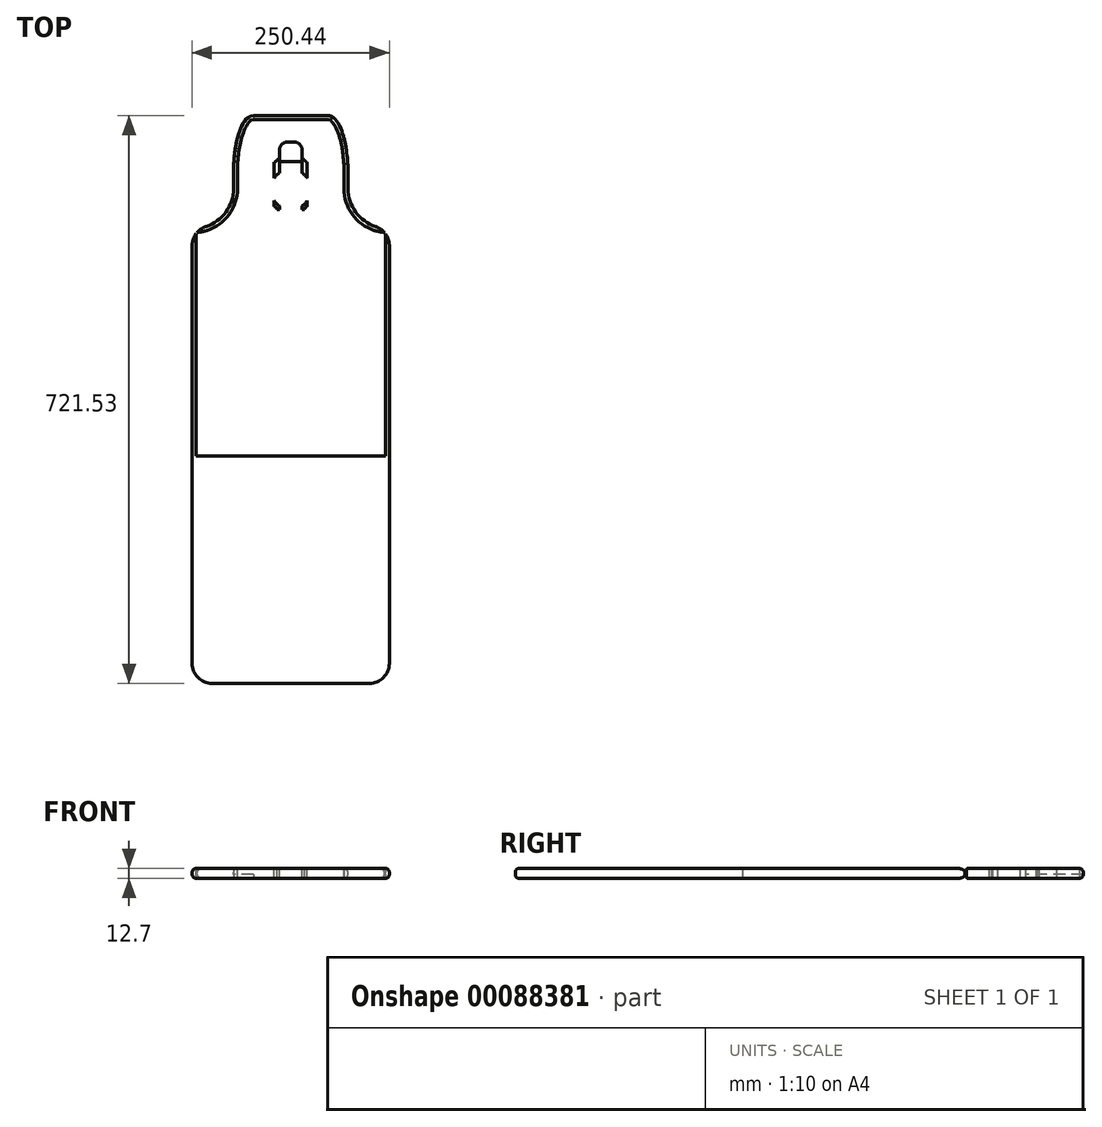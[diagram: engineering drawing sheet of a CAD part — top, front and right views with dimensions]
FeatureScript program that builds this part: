
annotation { "Feature Type Name" : "Feature", "Feature Type Description" : "" }
export const myFeature = defineFeature(function(context is Context, id is Id, definition is map)
    precondition{}
    {
        {
            var Q0;
            Q0=qCreatedBy(makeId("Top.planeOp"),FACE);
            var sketch = newSketch(context, id + "F0", { "sketchPlane" : qUnion([Q0])});
            skLineSegment(sketch, "E0.bottom", {"start": v(-117.17, 288.93) * mm, "end": v(-125.22, 288.93) * mm});
            skLineSegment(sketch, "E0.top", {"start": v(125.22, -288.93) * mm, "end": v(-125.22, -288.93) * mm});
            skLineSegment(sketch, "E0.left", {"start": v(125.22, 288.93) * mm, "end": v(125.22, -288.93) * mm});
            skLineSegment(sketch, "E0.right", {"start": v(-125.22, 288.93) * mm, "end": v(-125.22, -288.93) * mm});
            skPoint(sketch, "E0.middle", {"position": v(0, 0) * mm});
            skLineSegment(sketch, "E1", {"start": v(0, 308.77) * mm, "end": v(0, 432.6) * mm});
            skLineSegment(sketch, "E2.bottom", {"start": v(0, 432.6) * mm, "end": v(-47.32, 432.6) * mm});
            skLineSegment(sketch, "E2.right", {"start": v(-72.72, 360.76) * mm, "end": v(-72.72, 333.38) * mm});
            skLineSegment(sketch, "E3", {"start": v(0, 432.6) * mm, "end": v(0, 372.27) * mm});
            skLineSegment(sketch, "E4", {"start": v(-125.22, 0) * mm, "end": v(125.22, 0) * mm});
            skEllipticalArc(sketch, "E5", {});
            skPoint(sketch, "E6.newPointA", {"position": v(125.22, 288.93) * mm});
            skPoint(sketch, "E7.orphan", {"position": v(-72.72, 432.6) * mm});
            skLineSegment(sketch, "E8", {"start": v(125.22, 288.93) * mm, "end": v(117.17, 288.93) * mm});
            skPoint(sketch, "E2.left.start.orphan", {"position": v(72.72, 432.6) * mm});
            skEllipticalArc(sketch, "E9.MirrorCS", {});
            skLineSegment(sketch, "E10.MirrorCS", {"start": v(72.72, 360.76) * mm, "end": v(72.72, 333.38) * mm});
            skLineSegment(sketch, "E11.MirrorCS", {"start": v(0, 432.6) * mm, "end": v(47.32, 432.6) * mm});
            skLineSegment(sketch, "E12.MirrorCS", {"start": v(117.17, 288.93) * mm, "end": v(125.22, 288.93) * mm});
            skPoint(sketch, "E13.orphan", {"position": v(72.72, 288.93) * mm});
            skPoint(sketch, "E2.top.end.orphan", {"position": v(-72.72, 288.93) * mm});
            skLineSegment(sketch, "E14", {"start": v(-123.52, 288.93) * mm, "end": v(-117.17, 288.93) * mm});
            skLineSegment(sketch, "E15", {"start": v(-72.72, 333.38) * mm, "end": v(-72.72, 339.73) * mm});
            skLineSegment(sketch, "E16", {"start": v(117.17, 288.93) * mm, "end": v(123.52, 288.93) * mm});
            skLineSegment(sketch, "E17", {"start": v(72.72, 333.38) * mm, "end": v(72.72, 339.73) * mm});
            skArc(sketch, "E18.filletArc", {"start": v(-123.52, 288.92) * mm, "mid": v(-87.6, 303.8) * mm, "end": v(-72.72, 339.73) * mm});
            skArc(sketch, "E19.filletArc", {"start": v(72.72, 339.73) * mm, "mid": v(87.6, 303.8) * mm, "end": v(123.52, 288.93) * mm});
            skEllipticalArc(sketch, "E20.MirrorCS", {});
            skEllipticalArc(sketch, "E21.MirrorCS", {});
            skLineSegment(sketch, "E22.MirrorCS", {"start": v(72.72, -360.76) * mm, "end": v(72.72, -333.38) * mm});
            skArc(sketch, "E23.MirrorCS", {"start": v(72.72, -339.73) * mm, "mid": v(87.6, -303.8) * mm, "end": v(123.52, -288.92) * mm});
            skLineSegment(sketch, "E24.MirrorCS", {"start": v(117.17, -288.92) * mm, "end": v(123.52, -288.92) * mm});
            skLineSegment(sketch, "E25.MirrorCS", {"start": v(0, -432.6) * mm, "end": v(47.32, -432.6) * mm});
            skLineSegment(sketch, "E26.MirrorCS", {"start": v(0, -432.6) * mm, "end": v(-47.32, -432.6) * mm});
            skArc(sketch, "E27.MirrorCS", {"start": v(-123.52, -288.93) * mm, "mid": v(-87.6, -303.8) * mm, "end": v(-72.72, -339.73) * mm});
            skLineSegment(sketch, "E28.MirrorCS", {"start": v(-123.52, -288.93) * mm, "end": v(-117.17, -288.93) * mm});
            skLineSegment(sketch, "E29.MirrorCS", {"start": v(-117.17, -288.93) * mm, "end": v(-125.22, -288.93) * mm});
            skLineSegment(sketch, "E30.MirrorCS", {"start": v(-72.72, -360.76) * mm, "end": v(-72.72, -333.38) * mm});
            skLineSegment(sketch, "E31", {"start": v(-125.22, 288.93) * mm, "end": v(125.22, 288.93) * mm});
            const initialGuessF0  = {"E5": [-0.04731550595760356, 0.3607635015405606, 0, 1, 0.071834375, 0.0254, 0, 1.5707963267948966], "E9.MirrorCS": [0.04731550595760346, 0.3607635015405606, 0, 1, 0.071834375, 0.0254, 4.71238898038469, 0], "E20.MirrorCS": [-0.0473155059576034, -0.3607635015405606, 0, -1, 0.071834375, 0.0254, 4.71238898038469, 0], "E21.MirrorCS": [0.04731550595760362, -0.3607635015405606, 0, -1, 0.071834375, 0.0254, 0, 1.5707963267948966], "E20.MirrorCS": [-0.0473155059576034, -0.3607635015405606, 0, -1, 0.071834375, 0.0254, 4.71238898038469, 0], "E21.MirrorCS": [0.04731550595760362, -0.3607635015405606, 0, -1, 0.071834375, 0.0254, 0, 1.5707963267948966]};
            skSetInitialGuess(sketch, initialGuessF0);
            skSolve(sketch);
        }
        {
            var Q0;
            Q0=makeQuery(id+"F0.imprint","IMPRINT",FACE,{"disambiguationData":[TD([[makeQuery(id+"F0.imprint","IMPRINT",EDGE,{"derivedFrom":sQuery(id+"F0.wireOp",EDGE,"E2.bottom")}),1.0]])]});
            var Q1;
            {var subQ4=sQuery(id+"F0.wireOp",EDGE,"E4");Q1=makeQuery(id+"F0.imprint","IMPRINT",FACE,{"disambiguationData":[TD([[makeQuery(id+"F0.imprint","IMPRINT",EDGE,{"derivedFrom":subQ4}),1.0]])]});}
            var Q2;
            {var subQ3=sQuery(id+"F0.wireOp",EDGE,"E4");Q2=makeQuery(id+"F0.imprint","IMPRINT",FACE,{"disambiguationData":[TD([[makeQuery(id+"F0.imprint","IMPRINT",EDGE,{"derivedFrom":subQ3}),-1.0]])]});}
            var Q3;
            {var subQ6=sQuery(id+"F0.wireOp",EDGE,"E23.MirrorCS");Q3=makeQuery(id+"F0.imprint","IMPRINT",FACE,{"disambiguationData":[TD([[makeQuery(id+"F0.imprint","IMPRINT",EDGE,{"derivedFrom":subQ6}),1.0]])]});}
            extrude(context, id + "F1", {"entities" : qUnion([Q0, Q1, Q2, Q3]), "oppositeDirection" : true, "depth" : 12.7 * mm});
        }
        {
            var Q0;
            Q0=makeQuery(id+"F1.opExtrude","CAP_FACE",FACE,{"disambiguationData":[OSD([sQuery(id+"F0.wireOp",EDGE,"E0.top"),sQuery(id+"F0.wireOp",EDGE,"E0.left"),sQuery(id+"F0.wireOp",EDGE,"E0.right"),sQuery(id+"F0.wireOp",EDGE,"E2.bottom"),sQuery(id+"F0.wireOp",EDGE,"E2.right"),sQuery(id+"F0.wireOp",EDGE,"E5"),sQuery(id+"F0.wireOp",EDGE,"E9.MirrorCS"),sQuery(id+"F0.wireOp",EDGE,"E10.MirrorCS"),sQuery(id+"F0.wireOp",EDGE,"E11.MirrorCS"),sQuery(id+"F0.wireOp",EDGE,"E18.filletArc"),sQuery(id+"F0.wireOp",EDGE,"E19.filletArc"),sQuery(id+"F0.wireOp",EDGE,"E23.MirrorCS"),sQuery(id+"F0.wireOp",EDGE,"E25.MirrorCS"),sQuery(id+"F0.wireOp",EDGE,"E26.MirrorCS"),sQuery(id+"F0.wireOp",EDGE,"E20.MirrorCS"),sQuery(id+"F0.wireOp",EDGE,"E21.MirrorCS"),sQuery(id+"F0.wireOp",EDGE,"E22.MirrorCS"),sQuery(id+"F0.wireOp",EDGE,"E27.MirrorCS"),sQuery(id+"F0.wireOp",EDGE,"E29.MirrorCS"),sQuery(id+"F0.wireOp",EDGE,"E30.MirrorCS"),sQuery(id+"F0.wireOp",EDGE,"E31")])],"isStart":true});
            var Q1;
            Q1=makeQuery(id+"F1.opExtrude","CAP_FACE",FACE,{"disambiguationData":[OSD([sQuery(id+"F0.wireOp",EDGE,"E0.top"),sQuery(id+"F0.wireOp",EDGE,"E0.left"),sQuery(id+"F0.wireOp",EDGE,"E0.right"),sQuery(id+"F0.wireOp",EDGE,"E2.bottom"),sQuery(id+"F0.wireOp",EDGE,"E2.right"),sQuery(id+"F0.wireOp",EDGE,"E5"),sQuery(id+"F0.wireOp",EDGE,"E9.MirrorCS"),sQuery(id+"F0.wireOp",EDGE,"E10.MirrorCS"),sQuery(id+"F0.wireOp",EDGE,"E11.MirrorCS"),sQuery(id+"F0.wireOp",EDGE,"E18.filletArc"),sQuery(id+"F0.wireOp",EDGE,"E19.filletArc"),sQuery(id+"F0.wireOp",EDGE,"E23.MirrorCS"),sQuery(id+"F0.wireOp",EDGE,"E25.MirrorCS"),sQuery(id+"F0.wireOp",EDGE,"E26.MirrorCS"),sQuery(id+"F0.wireOp",EDGE,"E20.MirrorCS"),sQuery(id+"F0.wireOp",EDGE,"E21.MirrorCS"),sQuery(id+"F0.wireOp",EDGE,"E22.MirrorCS"),sQuery(id+"F0.wireOp",EDGE,"E27.MirrorCS"),sQuery(id+"F0.wireOp",EDGE,"E29.MirrorCS"),sQuery(id+"F0.wireOp",EDGE,"E30.MirrorCS"),sQuery(id+"F0.wireOp",EDGE,"E31")])],"isStart":false});
            fillet(context, id + "F2", {"entities" : qUnion([Q0, Q1]), "radius" : 5.08 * mm, "tangentPropagation" : true, "allowEdgeOverflow" : false});
        }
        {
            var Q0;
            Q0=makeQuery(id+"F1.opExtrude","CAP_FACE",FACE,{"disambiguationData":[OSD([sQuery(id+"F0.wireOp",EDGE,"E0.top"),sQuery(id+"F0.wireOp",EDGE,"E0.left"),sQuery(id+"F0.wireOp",EDGE,"E0.right"),sQuery(id+"F0.wireOp",EDGE,"E2.bottom"),sQuery(id+"F0.wireOp",EDGE,"E2.right"),sQuery(id+"F0.wireOp",EDGE,"E5"),sQuery(id+"F0.wireOp",EDGE,"E9.MirrorCS"),sQuery(id+"F0.wireOp",EDGE,"E10.MirrorCS"),sQuery(id+"F0.wireOp",EDGE,"E11.MirrorCS"),sQuery(id+"F0.wireOp",EDGE,"E18.filletArc"),sQuery(id+"F0.wireOp",EDGE,"E19.filletArc"),sQuery(id+"F0.wireOp",EDGE,"E23.MirrorCS"),sQuery(id+"F0.wireOp",EDGE,"E25.MirrorCS"),sQuery(id+"F0.wireOp",EDGE,"E26.MirrorCS"),sQuery(id+"F0.wireOp",EDGE,"E20.MirrorCS"),sQuery(id+"F0.wireOp",EDGE,"E21.MirrorCS"),sQuery(id+"F0.wireOp",EDGE,"E22.MirrorCS"),sQuery(id+"F0.wireOp",EDGE,"E27.MirrorCS"),sQuery(id+"F0.wireOp",EDGE,"E29.MirrorCS"),sQuery(id+"F0.wireOp",EDGE,"E30.MirrorCS"),sQuery(id+"F0.wireOp",EDGE,"E31")])],"isStart":true});
            var sketch = newSketch(context, id + "F3", { "sketchPlane" : qUnion([Q0])});
            skLineSegment(sketch, "E32", {"start": v(0, 427.52) * mm, "end": v(0, 376.72) * mm});
            skPoint(sketch, "E32.endSnap0", {"position": v(0, 427.52) * mm});
            skLineSegment(sketch, "E33", {"start": v(0, 376.72) * mm, "end": v(-20.96, 376.72) * mm});
            skLineSegment(sketch, "E34.bottom", {"start": v(-20.96, 376.72) * mm, "end": v(20.96, 376.72) * mm});
            skLineSegment(sketch, "E34.top", {"start": v(-20.95, 313.22) * mm, "end": v(20.96, 313.22) * mm});
            skLineSegment(sketch, "E34.left", {"start": v(-20.96, 376.72) * mm, "end": v(-20.96, 313.22) * mm});
            skLineSegment(sketch, "E34.right", {"start": v(20.96, 376.72) * mm, "end": v(20.96, 313.22) * mm});
            skLineSegment(sketch, "E35.0", {"start": v(-18.57, 374.34) * mm, "end": v(18.57, 374.34) * mm});
            skLineSegment(sketch, "E35.1", {"start": v(-18.57, 374.34) * mm, "end": v(-18.57, 315.6) * mm});
            skLineSegment(sketch, "E35.2", {"start": v(-18.57, 315.6) * mm, "end": v(18.57, 315.6) * mm});
            skLineSegment(sketch, "E35.3", {"start": v(18.57, 374.34) * mm, "end": v(18.57, 315.6) * mm});
            skCircle(sketch, "E36", {"center": v(-20.96, 376.72) * mm, "radius": 3.37 * mm});
            skCircle(sketch, "E37", {"center": v(20.96, 376.72) * mm, "radius": 3.37 * mm});
            skCircle(sketch, "E38", {"center": v(-20.95, 313.22) * mm, "radius": 3.37 * mm});
            skCircle(sketch, "E39", {"center": v(20.96, 313.22) * mm, "radius": 3.37 * mm});
            skLineSegment(sketch, "E40", {"start": v(-120.14, 0) * mm, "end": v(120.14, 0) * mm});
            skCircle(sketch, "E41.MirrorC", {"center": v(-20.95, -376.72) * mm, "radius": 3.37 * mm});
            skCircle(sketch, "E42.MirrorC", {"center": v(20.96, -313.22) * mm, "radius": 3.37 * mm});
            skCircle(sketch, "E43.MirrorC", {"center": v(-20.95, -313.22) * mm, "radius": 3.37 * mm});
            skCircle(sketch, "E44.MirrorC", {"center": v(20.96, -376.72) * mm, "radius": 3.37 * mm});
            skLineSegment(sketch, "E45", {"start": v(20.96, -313.22) * mm, "end": v(-20.95, -313.22) * mm});
            skLineSegment(sketch, "E46", {"start": v(0, -313.22) * mm, "end": v(0, -297.34) * mm});
            skLineSegment(sketch, "E47", {"start": v(0, -297.34) * mm, "end": v(-7.94, -297.34) * mm});
            skLineSegment(sketch, "E48", {"start": v(0, -297.34) * mm, "end": v(0, -398.94) * mm});
            skLineSegment(sketch, "E49", {"start": v(0, -398.94) * mm, "end": v(4.13, -398.94) * mm});
            skLineSegment(sketch, "E50.bottom", {"start": v(-7.94, -297.34) * mm, "end": v(7.94, -297.34) * mm});
            skLineSegment(sketch, "E50.top", {"start": v(-4.13, -398.94) * mm, "end": v(4.13, -398.94) * mm});
            skLineSegment(sketch, "E50.left", {"start": v(-14.29, -303.7) * mm, "end": v(-14.29, -317.62) * mm});
            skLineSegment(sketch, "E50.right", {"start": v(14.29, -303.7) * mm, "end": v(14.29, -317.62) * mm});
            skLineSegment(sketch, "E51", {"start": v(0, -313.22) * mm, "end": v(0, -338.62) * mm});
            skArc(sketch, "E52", {"start": v(-14.29, -317.62) * mm, "mid": v(-25.4, -338.62) * mm, "end": v(-14.29, -359.62) * mm});
            skArc(sketch, "E53.trimOffspring", {"start": v(14.29, -359.62) * mm, "mid": v(25.4, -338.62) * mm, "end": v(14.29, -317.62) * mm});
            skPoint(sketch, "E54.visualSharp", {"position": v(14.29, -398.94) * mm});
            skArc(sketch, "E54.filletArc", {"start": v(4.13, -398.94) * mm, "mid": v(11.31, -395.97) * mm, "end": v(14.29, -388.78) * mm});
            skPoint(sketch, "E55.visualSharp", {"position": v(-14.29, -398.94) * mm});
            skArc(sketch, "E55.filletArc", {"start": v(-14.29, -388.78) * mm, "mid": v(-11.31, -395.97) * mm, "end": v(-4.13, -398.94) * mm});
            skPoint(sketch, "E56.visualSharp", {"position": v(-14.29, -297.34) * mm});
            skArc(sketch, "E56.filletArc", {"start": v(-7.94, -297.34) * mm, "mid": v(-12.43, -299.2) * mm, "end": v(-14.29, -303.7) * mm});
            skPoint(sketch, "E57.visualSharp", {"position": v(14.29, -297.34) * mm});
            skArc(sketch, "E57.filletArc", {"start": v(14.29, -303.7) * mm, "mid": v(12.43, -299.2) * mm, "end": v(7.94, -297.34) * mm});
            skLineSegment(sketch, "E58.trimOffspring", {"start": v(14.29, -359.62) * mm, "end": v(14.29, -388.78) * mm});
            skLineSegment(sketch, "E59.trimOffspring", {"start": v(-14.29, -359.62) * mm, "end": v(-14.29, -388.78) * mm});
            skArc(sketch, "E60.MirrorCS", {"start": v(14.29, 359.62) * mm, "mid": v(25.4, 338.62) * mm, "end": v(14.29, 317.62) * mm});
            skArc(sketch, "E61.MirrorCS", {"start": v(-14.29, 317.62) * mm, "mid": v(-25.4, 338.62) * mm, "end": v(-14.29, 359.62) * mm});
            skLineSegment(sketch, "E62.MirrorCS", {"start": v(-14.29, 359.62) * mm, "end": v(-14.29, 388.78) * mm});
            skLineSegment(sketch, "E63.MirrorCS", {"start": v(14.29, 359.62) * mm, "end": v(14.29, 388.78) * mm});
            skArc(sketch, "E64.MirrorCS", {"start": v(4.13, 398.94) * mm, "mid": v(11.31, 395.97) * mm, "end": v(14.29, 388.78) * mm});
            skArc(sketch, "E65.MirrorCS", {"start": v(-14.29, 388.78) * mm, "mid": v(-11.31, 395.97) * mm, "end": v(-4.13, 398.94) * mm});
            skLineSegment(sketch, "E66.MirrorCS", {"start": v(-4.13, 398.94) * mm, "end": v(4.13, 398.94) * mm});
            skLineSegment(sketch, "E67.MirrorCS", {"start": v(-7.94, 297.34) * mm, "end": v(7.94, 297.34) * mm});
            skArc(sketch, "E68.MirrorCS", {"start": v(14.29, 303.7) * mm, "mid": v(12.43, 299.2) * mm, "end": v(7.94, 297.34) * mm});
            skArc(sketch, "E69.MirrorCS", {"start": v(-7.94, 297.34) * mm, "mid": v(-12.43, 299.2) * mm, "end": v(-14.29, 303.7) * mm});
            skLineSegment(sketch, "E70.MirrorCS", {"start": v(-14.29, 303.7) * mm, "end": v(-14.29, 317.62) * mm});
            skLineSegment(sketch, "E71.MirrorCS", {"start": v(14.29, 303.7) * mm, "end": v(14.29, 317.62) * mm});
            skSolve(sketch);
        }
        {
            var Q0;
            Q0=sQuery(id+"F3.wireOp",VERTEX,"3598a4d0-b501-495c-ae59-4652df5df4007.MirrorCS.end");
            var Q1;
            Q1=sQuery(id+"F3.wireOp",VERTEX,"3598a4d0-b501-495c-ae59-4652df5df4008.MirrorCS.end");
            var Q2;
            Q2=sQuery(id+"F3.wireOp",VERTEX,"3598a4d0-b501-495c-ae59-4652df5df4004.MirrorCS.end");
            var Q3;
            Q3=sQuery(id+"F3.wireOp",VERTEX,"3598a4d0-b501-495c-ae59-4652df5df4009.MirrorCS.start");
            var Q4;
            Q4=sQuery(id+"F3.wireOp",VERTEX,"E37.center");
            var Q5;
            Q5=sQuery(id+"F3.wireOp",VERTEX,"E34.left.start");
            var Q6;
            Q6=sQuery(id+"F3.wireOp",VERTEX,"E38.center");
            var Q7;
            Q7=sQuery(id+"F3.wireOp",VERTEX,"E34.right.end");
            var Q8;
            Q8=sQuery(id+"F3.wireOp",VERTEX,"E42.MirrorC.center");
            var Q9;
            Q9=sQuery(id+"F3.wireOp",VERTEX,"E43.MirrorC.center");
            var Q10;
            Q10=sQuery(id+"F3.wireOp",VERTEX,"E44.MirrorC.center");
            var Q11;
            Q11=sQuery(id+"F3.wireOp",VERTEX,"E41.MirrorC.center");
            var Q12;
            Q12=makeQuery(id+"F1.opExtrude","SWEPT_BODY",BODY,{"disambiguationData":[OSD([sQuery(id+"F0.wireOp",EDGE,"E0.top"),sQuery(id+"F0.wireOp",EDGE,"E0.left"),sQuery(id+"F0.wireOp",EDGE,"E0.right"),sQuery(id+"F0.wireOp",EDGE,"E2.bottom"),sQuery(id+"F0.wireOp",EDGE,"E2.right"),sQuery(id+"F0.wireOp",EDGE,"E5"),sQuery(id+"F0.wireOp",EDGE,"E9.MirrorCS"),sQuery(id+"F0.wireOp",EDGE,"E10.MirrorCS"),sQuery(id+"F0.wireOp",EDGE,"E11.MirrorCS"),sQuery(id+"F0.wireOp",EDGE,"E18.filletArc"),sQuery(id+"F0.wireOp",EDGE,"E19.filletArc"),sQuery(id+"F0.wireOp",EDGE,"E23.MirrorCS"),sQuery(id+"F0.wireOp",EDGE,"E25.MirrorCS"),sQuery(id+"F0.wireOp",EDGE,"E26.MirrorCS"),sQuery(id+"F0.wireOp",EDGE,"E20.MirrorCS"),sQuery(id+"F0.wireOp",EDGE,"E21.MirrorCS"),sQuery(id+"F0.wireOp",EDGE,"E22.MirrorCS"),sQuery(id+"F0.wireOp",EDGE,"E27.MirrorCS"),sQuery(id+"F0.wireOp",EDGE,"E29.MirrorCS"),sQuery(id+"F0.wireOp",EDGE,"E30.MirrorCS"),sQuery(id+"F0.wireOp",EDGE,"E31")])]});
            hole(context, id + "F4", {"style" : HoleStyle.SIMPLE, "endStyle" : HoleEndStyle.THROUGH, "standardTappedOrClearance" : lookupTablePath({ "standard" : "ANSI", "fit" : "Normal (ASME)", "size" : "1/4", "type" : "Clearance" }), "standardBlindInLast" : lookupTablePath({ "fit" : "Free", "standard" : "ANSI", "size" : "1/4", "type" : "Clearance" }), "holeDiameter" : 6.76 * mm, "locations" : qUnion([Q0, Q1, Q2, Q3, Q4, Q5, Q6, Q7, Q8, Q9, Q10, Q11]), "scope" : qUnion([Q12]), "isTappedThrough" : true});
        }
        {
            var Q0;
            Q0=makeQuery(id+"F1.opExtrude","SWEPT_EDGE",EDGE,{"disambiguationData":[OSD([sQuery(id+"F0.wireOp",EDGE,"E0.right"),sQuery(id+"F0.wireOp",EDGE,"E31")])]});
            var Q1;
            Q1=makeQuery(id+"F1.opExtrude","SWEPT_EDGE",EDGE,{"disambiguationData":[OSD([sQuery(id+"F0.wireOp",EDGE,"E0.left"),sQuery(id+"F0.wireOp",EDGE,"E31")])]});
            var Q2;
            Q2=makeQuery(id+"F1.opExtrude","SWEPT_EDGE",EDGE,{"disambiguationData":[OSD([sQuery(id+"F0.wireOp",EDGE,"E0.top"),sQuery(id+"F0.wireOp",EDGE,"E0.left")])]});
            var Q3;
            Q3=makeQuery(id+"F1.opExtrude","SWEPT_EDGE",EDGE,{"disambiguationData":[OSD([sQuery(id+"F0.wireOp",EDGE,"E0.right"),sQuery(id+"F0.wireOp",EDGE,"E29.MirrorCS")])]});
            fillet(context, id + "F5", {"entities" : qUnion([Q0, Q1, Q2, Q3]), "radius" : 25.4 * mm, "tangentPropagation" : true, "allowEdgeOverflow" : false});
        }
        {
            var Q0;
            {var subQ3=sQuery(id+"F3.wireOp",EDGE,"E35.0");var subQ5=sQuery(id+"F3.wireOp",EDGE,"E62.MirrorCS");var subQ8=makeQuery(id+"F3.imprint","INTERSECT",VERTEX,{"derivedFrom":[subQ3,subQ5]});Q0=makeQuery(id+"F3.imprint","IMPRINT",FACE,{"disambiguationData":[TD([[makeQuery(id+"F3.imprint","IMPRINT",EDGE,{"disambiguationData":[TD([[subQ8,-1.0]])],"derivedFrom":subQ3}),-1.0]])]});}
            var Q1;
            {var subQ1=sQuery(id+"F3.wireOp",EDGE,"E34.bottom");var subQ5=makeQuery(id+"F3.imprint","INTERSECT",VERTEX,{"derivedFrom":[sQuery(id+"F3.wireOp",EDGE,"E32"),subQ1]});Q1=makeQuery(id+"F3.imprint","IMPRINT",FACE,{"disambiguationData":[TD([[makeQuery(id+"F3.imprint","IMPRINT",EDGE,{"disambiguationData":[TD([[subQ5,1.0]])],"derivedFrom":subQ1}),-1.0]])]});}
            var Q2;
            {var subQ0=sQuery(id+"F3.wireOp",EDGE,"E64.MirrorCS");Q2=makeQuery(id+"F3.imprint","IMPRINT",FACE,{"disambiguationData":[TD([[makeQuery(id+"F3.imprint","IMPRINT",EDGE,{"derivedFrom":subQ0}),-1.0]])]});}
            var Q3;
            {var subQ0=sQuery(id+"F3.wireOp",EDGE,"E65.MirrorCS");Q3=makeQuery(id+"F3.imprint","IMPRINT",FACE,{"disambiguationData":[TD([[makeQuery(id+"F3.imprint","IMPRINT",EDGE,{"derivedFrom":subQ0}),-1.0]])]});}
            var Q4;
            {var subQ0=sQuery(id+"F3.wireOp",EDGE,"E60.MirrorCS");var subQ1=sQuery(id+"F3.wireOp",EDGE,"E34.right");var subQ2=makeQuery(id+"F3.imprint","INTERSECT",VERTEX,{"disambiguationData":[OD(0.0)],"derivedFrom":[subQ1,subQ0]});Q4=makeQuery(id+"F3.imprint","IMPRINT",FACE,{"disambiguationData":[TD([[makeQuery(id+"F3.imprint","IMPRINT",EDGE,{"disambiguationData":[TD([[subQ2,-1.0]])],"derivedFrom":subQ1}),-1.0]])]});}
            var Q5;
            {var subQ0=sQuery(id+"F3.wireOp",EDGE,"E60.MirrorCS");var subQ1=sQuery(id+"F3.wireOp",EDGE,"E34.right");var subQ2=makeQuery(id+"F3.imprint","INTERSECT",VERTEX,{"disambiguationData":[OD(0.0)],"derivedFrom":[subQ1,subQ0]});Q5=makeQuery(id+"F3.imprint","IMPRINT",FACE,{"disambiguationData":[TD([[makeQuery(id+"F3.imprint","IMPRINT",EDGE,{"disambiguationData":[TD([[subQ2,-1.0]])],"derivedFrom":subQ1}),1.0]])]});}
            var Q6;
            {var subQ0=sQuery(id+"F3.wireOp",EDGE,"E61.MirrorCS");var subQ1=sQuery(id+"F3.wireOp",EDGE,"E34.left");var subQ2=makeQuery(id+"F3.imprint","INTERSECT",VERTEX,{"disambiguationData":[OD(0.0)],"derivedFrom":[subQ1,subQ0]});Q6=makeQuery(id+"F3.imprint","IMPRINT",FACE,{"disambiguationData":[TD([[makeQuery(id+"F3.imprint","IMPRINT",EDGE,{"disambiguationData":[TD([[subQ2,-1.0]])],"derivedFrom":subQ1}),1.0]])]});}
            var Q7;
            {var subQ0=sQuery(id+"F3.wireOp",EDGE,"E61.MirrorCS");var subQ1=sQuery(id+"F3.wireOp",EDGE,"E34.left");var subQ2=makeQuery(id+"F3.imprint","INTERSECT",VERTEX,{"disambiguationData":[OD(0.0)],"derivedFrom":[subQ1,subQ0]});Q7=makeQuery(id+"F3.imprint","IMPRINT",FACE,{"disambiguationData":[TD([[makeQuery(id+"F3.imprint","IMPRINT",EDGE,{"disambiguationData":[TD([[subQ2,-1.0]])],"derivedFrom":subQ1}),-1.0]])]});}
            var Q8;
            Q8=makeQuery(id+"F3.imprint","IMPRINT",FACE,{"disambiguationData":[TD([[makeQuery(id+"F3.imprint","IMPRINT",EDGE,{"derivedFrom":sQuery(id+"F3.wireOp",EDGE,"E67.MirrorCS")}),1.0]])]});
            var Q9;
            {var subQ0=sQuery(id+"F3.wireOp",EDGE,"E70.MirrorCS");var subQ1=sQuery(id+"F3.wireOp",EDGE,"E34.top");var subQ2=makeQuery(id+"F3.imprint","INTERSECT",VERTEX,{"derivedFrom":[subQ1,subQ0]});Q9=makeQuery(id+"F3.imprint","IMPRINT",FACE,{"disambiguationData":[TD([[makeQuery(id+"F3.imprint","IMPRINT",EDGE,{"disambiguationData":[TD([[subQ2,-1.0]])],"derivedFrom":subQ1}),1.0]])]});}
            var Q10;
            {var subQ4=sQuery(id+"F3.wireOp",EDGE,"E51");Q10=makeQuery(id+"F3.imprint","IMPRINT",FACE,{"disambiguationData":[TD([[makeQuery(id+"F3.imprint","IMPRINT",EDGE,{"derivedFrom":subQ4}),1.0]])]});}
            var Q11;
            {var subQ4=sQuery(id+"F3.wireOp",EDGE,"E51");Q11=makeQuery(id+"F3.imprint","IMPRINT",FACE,{"disambiguationData":[TD([[makeQuery(id+"F3.imprint","IMPRINT",EDGE,{"derivedFrom":subQ4}),-1.0]])]});}
            var Q12;
            {var subQ0=sQuery(id+"F3.wireOp",EDGE,"E56.filletArc");Q12=makeQuery(id+"F3.imprint","IMPRINT",FACE,{"disambiguationData":[TD([[makeQuery(id+"F3.imprint","IMPRINT",EDGE,{"derivedFrom":subQ0}),1.0]])]});}
            var Q13;
            {var subQ0=sQuery(id+"F3.wireOp",EDGE,"E57.filletArc");Q13=makeQuery(id+"F3.imprint","IMPRINT",FACE,{"disambiguationData":[TD([[makeQuery(id+"F3.imprint","IMPRINT",EDGE,{"derivedFrom":subQ0}),1.0]])]});}
            extrude(context, id + "F6", {"entities" : qUnion([Q0, Q1, Q2, Q3, Q4, Q5, Q6, Q7, Q8, Q9, Q10, Q11, Q12, Q13]), "operationType" : NewBodyOperationType.REMOVE, "endBound" : BoundingType.THROUGH_ALL, "oppositeDirection" : true, "depth" : 25.4 * mm});
        }
    });
